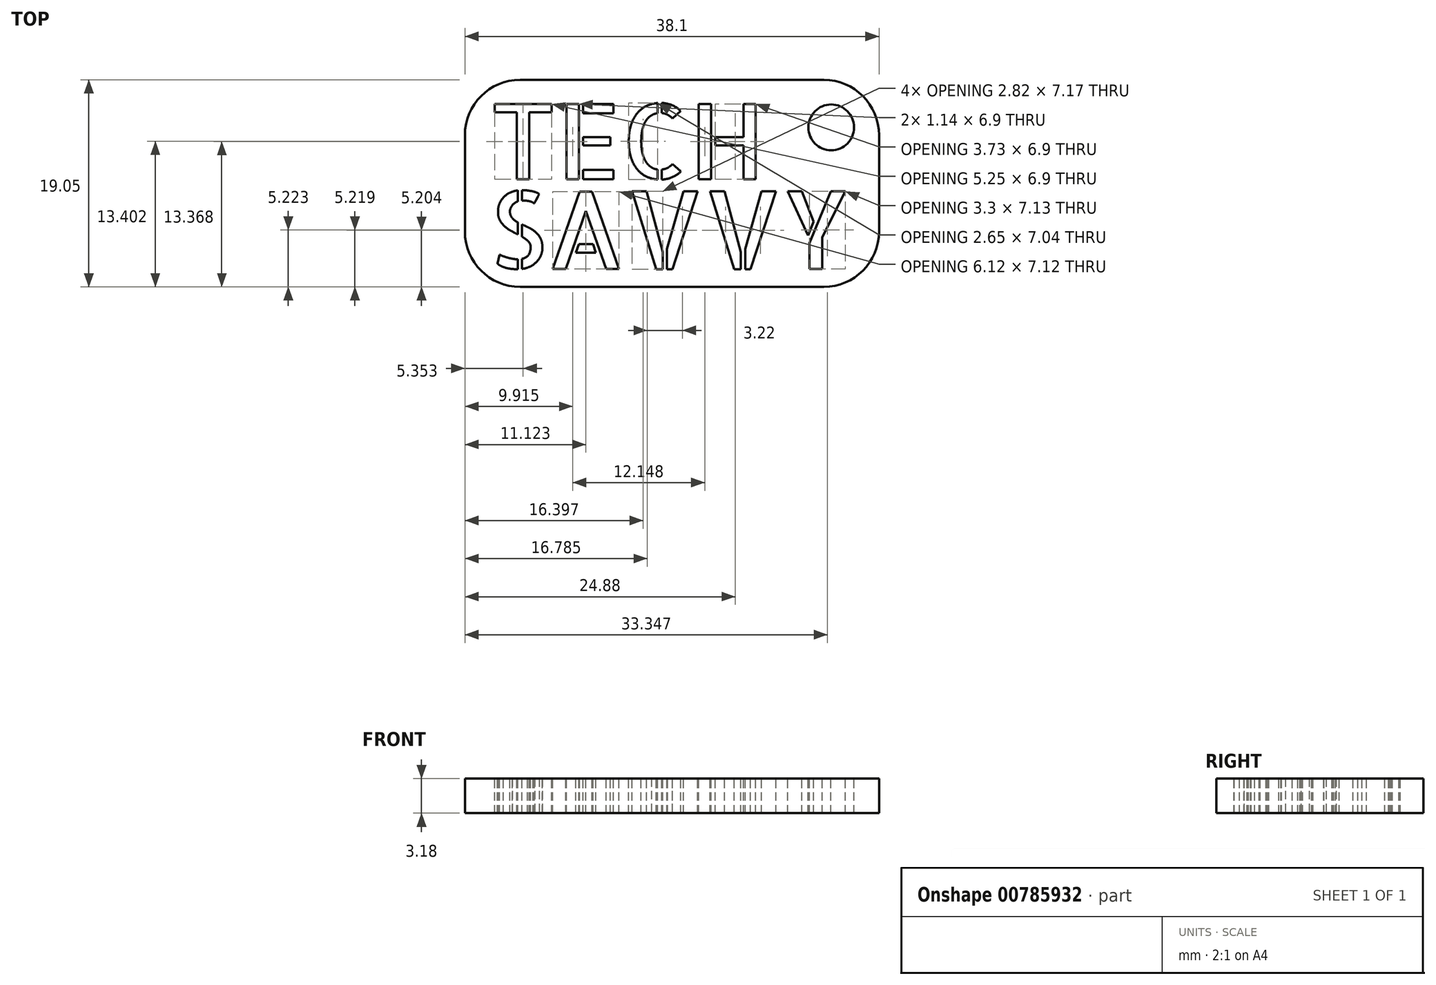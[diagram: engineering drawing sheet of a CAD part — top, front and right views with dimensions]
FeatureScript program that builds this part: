
annotation { "Feature Type Name" : "Feature", "Feature Type Description" : "" }
export const myFeature = defineFeature(function(context is Context, id is Id, definition is map)
    precondition{}
    {
        {
            var Q0;
            Q0=qCreatedBy(makeId("Top.planeOp"),FACE);
            var sketch = newSketch(context, id + "F0", { "sketchPlane" : qUnion([Q0])});
            skLineSegment(sketch, "E0.bottom", {"start": v(0, 0) * mm, "end": v(38.1, 0) * mm});
            skLineSegment(sketch, "E0.top", {"start": v(0, 19.05) * mm, "end": v(38.1, 19.05) * mm});
            skLineSegment(sketch, "E0.left", {"start": v(0, 0) * mm, "end": v(0, 19.05) * mm});
            skLineSegment(sketch, "E0.right", {"start": v(38.1, 0) * mm, "end": v(38.1, 19.05) * mm});
            skSolve(sketch);
        }
        {
            var Q0;
            Q0=makeQuery(id+"F0.imprint","IMPRINT",FACE,{"disambiguationData":[TD([[makeQuery(id+"F0.imprint","IMPRINT",EDGE,{"derivedFrom":sQuery(id+"F0.wireOp",EDGE,"E0.bottom")}),1.0]])]});
            extrude(context, id + "F1", {"entities" : qUnion([Q0]), "oppositeDirection" : true, "depth" : 3.17 * mm, "offsetDistance" : 25.4 * mm});
        }
        {
            var Q0;
            Q0=makeQuery(id+"F1.opExtrude","CAP_FACE",FACE,{"disambiguationData":[OSD([sQuery(id+"F0.wireOp",EDGE,"E0.bottom"),sQuery(id+"F0.wireOp",EDGE,"E0.top"),sQuery(id+"F0.wireOp",EDGE,"E0.left"),sQuery(id+"F0.wireOp",EDGE,"E0.right")])],"isStart":true});
            var sketch = newSketch(context, id + "F2", { "sketchPlane" : qUnion([Q0])});
            skText(sketch, "E1", { "text": "TECH", "fontName": "AllertaStencil-Regular.ttf"});
            skText(sketch, "E2", { "text": "SAVVY", "fontName": "AllertaStencil-Regular.ttf"});
            skCircle(sketch, "E3", {"center": v(33.7, 14.68) * mm, "radius": 2.1 * mm});
            const initialGuessF2  = {"E1": [0.00225, 0.00992, 1, 0, 0.0069], "E2": [0.00221, 0.00166, 1, 0, 0.00713]};
            skSetInitialGuess(sketch, initialGuessF2);
            skSolve(sketch);
        }
        {
            var Q0;
            Q0=makeQuery(id+"F2.imprint","IMPRINT",FACE,{"disambiguationData":[TD([[makeQuery(id+"F2.imprint","IMPRINT",EDGE,{"derivedFrom":sQuery(id+"F2.wireOp",EDGE,"E1.sketch_text.stroke-0")}),-1.0]])]});
            var Q1;
            Q1=makeQuery(id+"F2.imprint","IMPRINT",FACE,{"disambiguationData":[TD([[makeQuery(id+"F2.imprint","IMPRINT",EDGE,{"derivedFrom":sQuery(id+"F2.wireOp",EDGE,"E1.sketch_text.stroke-8")}),-1.0]])]});
            var Q2;
            Q2=makeQuery(id+"F2.imprint","IMPRINT",FACE,{"disambiguationData":[TD([[makeQuery(id+"F2.imprint","IMPRINT",EDGE,{"derivedFrom":sQuery(id+"F2.wireOp",EDGE,"E1.sketch_text.stroke-20")}),-1.0]])]});
            var Q3;
            Q3=makeQuery(id+"F2.imprint","IMPRINT",FACE,{"disambiguationData":[TD([[makeQuery(id+"F2.imprint","IMPRINT",EDGE,{"derivedFrom":sQuery(id+"F2.wireOp",EDGE,"E1.sketch_text.stroke-12")}),-1.0]])]});
            var Q4;
            Q4=makeQuery(id+"F2.imprint","IMPRINT",FACE,{"disambiguationData":[TD([[makeQuery(id+"F2.imprint","IMPRINT",EDGE,{"derivedFrom":sQuery(id+"F2.wireOp",EDGE,"E1.sketch_text.stroke-16")}),-1.0]])]});
            var Q5;
            Q5=makeQuery(id+"F2.imprint","IMPRINT",FACE,{"disambiguationData":[TD([[makeQuery(id+"F2.imprint","IMPRINT",EDGE,{"derivedFrom":sQuery(id+"F2.wireOp",EDGE,"E1.sketch_text.stroke-35")}),-1.0]])]});
            var Q6;
            Q6=makeQuery(id+"F2.imprint","IMPRINT",FACE,{"disambiguationData":[TD([[makeQuery(id+"F2.imprint","IMPRINT",EDGE,{"derivedFrom":sQuery(id+"F2.wireOp",EDGE,"E1.sketch_text.stroke-29")}),-1.0]])]});
            var Q7;
            Q7=makeQuery(id+"F2.imprint","IMPRINT",FACE,{"disambiguationData":[TD([[makeQuery(id+"F2.imprint","IMPRINT",EDGE,{"derivedFrom":sQuery(id+"F2.wireOp",EDGE,"E1.sketch_text.stroke-24")}),-1.0]])]});
            var Q8;
            Q8=makeQuery(id+"F2.imprint","IMPRINT",FACE,{"disambiguationData":[TD([[makeQuery(id+"F2.imprint","IMPRINT",EDGE,{"derivedFrom":sQuery(id+"F2.wireOp",EDGE,"E1.sketch_text.stroke-61")}),-1.0]])]});
            var Q9;
            Q9=makeQuery(id+"F2.imprint","IMPRINT",FACE,{"disambiguationData":[TD([[makeQuery(id+"F2.imprint","IMPRINT",EDGE,{"derivedFrom":sQuery(id+"F2.wireOp",EDGE,"E1.sketch_text.stroke-53")}),-1.0]])]});
            var Q10;
            Q10=makeQuery(id+"F2.imprint","IMPRINT",FACE,{"disambiguationData":[TD([[makeQuery(id+"F2.imprint","IMPRINT",EDGE,{"derivedFrom":sQuery(id+"F2.wireOp",EDGE,"E2.sketch_text.stroke-11")}),-1.0]])]});
            var Q11;
            Q11=makeQuery(id+"F2.imprint","IMPRINT",FACE,{"disambiguationData":[TD([[makeQuery(id+"F2.imprint","IMPRINT",EDGE,{"derivedFrom":sQuery(id+"F2.wireOp",EDGE,"E2.sketch_text.stroke-37")}),-1.0]])]});
            var Q12;
            Q12=makeQuery(id+"F2.imprint","IMPRINT",FACE,{"disambiguationData":[TD([[makeQuery(id+"F2.imprint","IMPRINT",EDGE,{"derivedFrom":sQuery(id+"F2.wireOp",EDGE,"E2.sketch_text.stroke-25")}),-1.0]])]});
            var Q13;
            Q13=makeQuery(id+"F2.imprint","IMPRINT",FACE,{"disambiguationData":[TD([[makeQuery(id+"F2.imprint","IMPRINT",EDGE,{"derivedFrom":sQuery(id+"F2.wireOp",EDGE,"E2.sketch_text.stroke-0")}),-1.0]])]});
            var Q14;
            Q14=makeQuery(id+"F2.imprint","IMPRINT",FACE,{"disambiguationData":[TD([[makeQuery(id+"F2.imprint","IMPRINT",EDGE,{"derivedFrom":sQuery(id+"F2.wireOp",EDGE,"E2.sketch_text.stroke-50")}),-1.0]])]});
            var Q15;
            Q15=makeQuery(id+"F2.imprint","IMPRINT",FACE,{"disambiguationData":[TD([[makeQuery(id+"F2.imprint","IMPRINT",EDGE,{"derivedFrom":sQuery(id+"F2.wireOp",EDGE,"E2.sketch_text.stroke-57")}),-1.0]])]});
            var Q16;
            Q16=makeQuery(id+"F2.imprint","IMPRINT",FACE,{"disambiguationData":[TD([[makeQuery(id+"F2.imprint","IMPRINT",EDGE,{"derivedFrom":sQuery(id+"F2.wireOp",EDGE,"E2.sketch_text.stroke-61")}),-1.0]])]});
            var Q17;
            Q17=makeQuery(id+"F2.imprint","IMPRINT",FACE,{"disambiguationData":[TD([[makeQuery(id+"F2.imprint","IMPRINT",EDGE,{"derivedFrom":sQuery(id+"F2.wireOp",EDGE,"E2.sketch_text.stroke-66")}),-1.0]])]});
            var Q18;
            Q18=makeQuery(id+"F2.imprint","IMPRINT",FACE,{"disambiguationData":[TD([[makeQuery(id+"F2.imprint","IMPRINT",EDGE,{"derivedFrom":sQuery(id+"F2.wireOp",EDGE,"E2.sketch_text.stroke-71")}),-1.0]])]});
            var Q19;
            Q19=makeQuery(id+"F2.imprint","IMPRINT",FACE,{"disambiguationData":[TD([[makeQuery(id+"F2.imprint","IMPRINT",EDGE,{"derivedFrom":sQuery(id+"F2.wireOp",EDGE,"E2.sketch_text.stroke-76")}),-1.0]])]});
            var Q20;
            Q20=makeQuery(id+"F2.imprint","IMPRINT",FACE,{"disambiguationData":[TD([[makeQuery(id+"F2.imprint","IMPRINT",EDGE,{"derivedFrom":sQuery(id+"F2.wireOp",EDGE,"E2.sketch_text.stroke-87")}),-1.0]])]});
            var Q21;
            Q21=makeQuery(id+"F2.imprint","IMPRINT",FACE,{"disambiguationData":[TD([[makeQuery(id+"F2.imprint","IMPRINT",EDGE,{"derivedFrom":sQuery(id+"F2.wireOp",EDGE,"E2.sketch_text.stroke-81")}),-1.0]])]});
            var Q22;
            Q22=makeQuery(id+"F2.imprint","IMPRINT",FACE,{"disambiguationData":[TD([[makeQuery(id+"F2.imprint","IMPRINT",EDGE,{"derivedFrom":sQuery(id+"F2.wireOp",EDGE,"E3")}),1.0]])]});
            extrude(context, id + "F3", {"entities" : qUnion([Q0, Q1, Q2, Q3, Q4, Q5, Q6, Q7, Q8, Q9, Q10, Q11, Q12, Q13, Q14, Q15, Q16, Q17, Q18, Q19, Q20, Q21, Q22]), "operationType" : NewBodyOperationType.REMOVE, "endBound" : BoundingType.THROUGH_ALL, "oppositeDirection" : true, "depth" : 25.4 * mm, "offsetDistance" : 25.4 * mm});
        }
        {
            var Q0;
            Q0=makeQuery(id+"F1.opExtrude","SWEPT_EDGE",EDGE,{"disambiguationData":[OSD([sQuery(id+"F0.wireOp",EDGE,"E0.bottom"),sQuery(id+"F0.wireOp",EDGE,"E0.left")])]});
            var Q1;
            Q1=makeQuery(id+"F1.opExtrude","SWEPT_EDGE",EDGE,{"disambiguationData":[OSD([sQuery(id+"F0.wireOp",EDGE,"E0.bottom"),sQuery(id+"F0.wireOp",EDGE,"E0.right")])]});
            var Q2;
            Q2=makeQuery(id+"F1.opExtrude","SWEPT_EDGE",EDGE,{"disambiguationData":[OSD([sQuery(id+"F0.wireOp",EDGE,"E0.top"),sQuery(id+"F0.wireOp",EDGE,"E0.right")])]});
            var Q3;
            Q3=makeQuery(id+"F1.opExtrude","SWEPT_EDGE",EDGE,{"disambiguationData":[OSD([sQuery(id+"F0.wireOp",EDGE,"E0.top"),sQuery(id+"F0.wireOp",EDGE,"E0.left")])]});
            fillet(context, id + "F4", {"entities" : qUnion([Q0, Q1, Q2, Q3]), "radius" : 5.08 * mm, "tangentPropagation" : true, "allowEdgeOverflow" : false});
        }
    });
